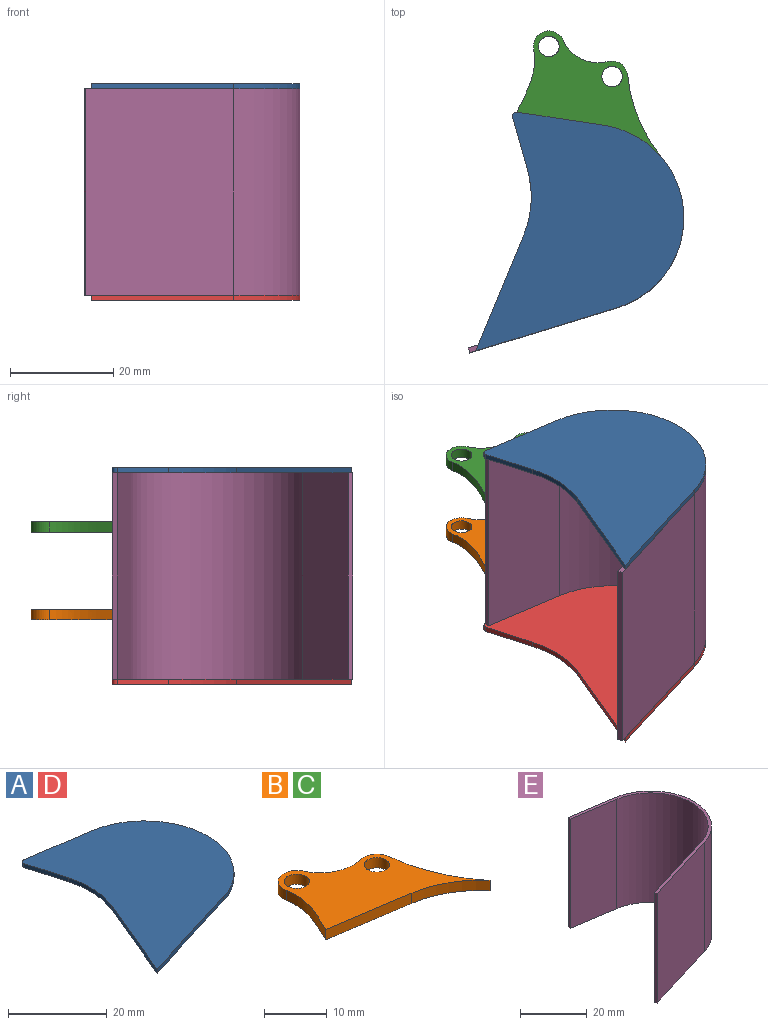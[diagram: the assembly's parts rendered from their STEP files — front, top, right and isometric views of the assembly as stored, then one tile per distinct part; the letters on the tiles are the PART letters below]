
ASSEMBLY  parts=5 mates=4
PART A: 9 faces, bbox 40.3x46.3x1 mm
  f0: plane 16.93x2.57mm, normal (0.15,0.99,0), area 17.1mm2, adj f1,f6,f7,f8
  f1: cylinder r=0.75mm len=1mm, axis (0,0,-1), area 1.5mm2, adj f0,f2,f7,f8
  f2: plane 9.96x2.84mm, normal (-0.96,-0.27,0), area 10.4mm2, adj f1,f3,f7,f8
  f3: cylinder r=20mm len=13.14mm, axis (0,0,-1), area 13.4mm2, adj f2,f4,f7,f8
  f4: plane 22.22x9.21mm, normal (-0.92,0.38,0), area 24.1mm2, adj f3,f5,f7,f8
  f5: plane 27.49x8.41mm, normal (0.29,-0.96,0), area 28.7mm2, adj f4,f6,f7,f8
  f6: cylinder r=18.15mm len=35.3mm, axis (0,0,-1), area 48.9mm2, adj f0,f5,f7,f8
  f7: plane 46.28x40.33mm, normal (0,0,1), area 1124.3mm2, adj f0,f1,f2,f3,f4,f5,f6
  f8: plane 46.28x40.33mm, normal (0,0,-1), area 1124.3mm2, adj f0,f1,f2,f3,f4,f5,f6
PART B: 11 faces, bbox 28.2x24.7x2 mm
  f0: cylinder r=18.15mm len=11.26mm, axis (0,0,-1), area 26.5mm2, adj f1,f6,f7,f8
  f1: cylinder r=30mm len=16.15mm, axis (0,0,-1), area 35.5mm2, adj f0,f2,f7,f8
  f2: cylinder r=3mm len=3.75mm, axis (0,0,-1), area 10.4mm2, adj f1,f3,f7,f8
  f3: cylinder r=7.5mm len=8.76mm, axis (0,0,-1), area 21.1mm2, adj f2,f4,f7,f8
  f4: cylinder r=3mm len=5.74mm, axis (0,0,-1), area 17.5mm2, adj f3,f5,f7,f8
  f5: extruded ~12.19x3.44mm, area 25.7mm2, adj f4,f6,f7,f8
  f6: plane 16.93x2.57mm, normal (-0.15,-0.99,0), area 34.2mm2, adj f0,f5,f7,f8
  f7: plane 28.19x24.69mm, normal (0,0,1), area 255.1mm2, adj f0,f1,f2,f3,f4,f5,f6,f9
  f8: plane 28.19x24.69mm, normal (0,0,-1), area 255.1mm2, adj f0,f1,f2,f3,f4,f5,f6,f9
  f9: cylinder r=2mm len=4mm, axis (0,0,-1), area 25.1mm2, adj f7,f8
  f10: cylinder r=2mm len=4mm, axis (0,0,-1), area 25.1mm2, adj f7,f8
PART C: same geometry as B
PART D: same geometry as A
PART E: 10 faces, bbox 41.8x46.6x40 mm
  f0: cylinder r=18.15mm len=40mm, axis (0,0,-1), area 1955.7mm2, adj f1,f7,f8,f9
  f1: plane 40x16.93mm, normal (0.15,0.99,0), area 685mm2, adj f0,f2,f8,f9
  f2: plane 40x0.99mm, normal (-0.99,0.15,0), area 40mm2, adj f1,f3,f8,f9
  f3: plane 40x16.93mm, normal (-0.15,-0.99,0), area 685mm2, adj f2,f4,f8,f9
  f4: cylinder r=17.15mm len=40mm, axis (0,0,-1), area 1848mm2, adj f3,f5,f8,f9
  f5: plane 40x28.65mm, normal (-0.29,0.96,0), area 1198.4mm2, adj f4,f6,f8,f9
  f6: plane 40x0.96mm, normal (-0.96,-0.29,0), area 40mm2, adj f5,f7,f8,f9
  f7: plane 40x28.65mm, normal (0.29,-0.96,0), area 1198.4mm2, adj f0,f6,f8,f9
  f8: plane 46.63x41.78mm, normal (0,0,1), area 94.6mm2, adj f0,f1,f2,f3,f4,f5,f6,f7
  f9: plane 46.63x41.78mm, normal (0,0,-1), area 94.6mm2, adj f0,f1,f2,f3,f4,f5,f6,f7
PLACE A t=(0,0,40)mm
PLACE B t=(0,0,11.5)mm
PLACE C t=(0,0,28.5)mm
PLACE D t=(0,0,-1)mm
PLACE E at identity
MATE fastened B.f0 <-> E.f0  axis (0,0,1) through (23.34,26.57,13.5)mm
MATE fastened A.f6 <-> E.f0  axis (0,0,-1) through (23.34,26.57,40)mm
MATE fastened B.f2 <-> C.f2  axis (0,0,1) through (27.59,54,13.5)mm
MATE fastened D.f6 <-> E.f0  axis (0,0,1) through (23.34,26.57,0)mm
